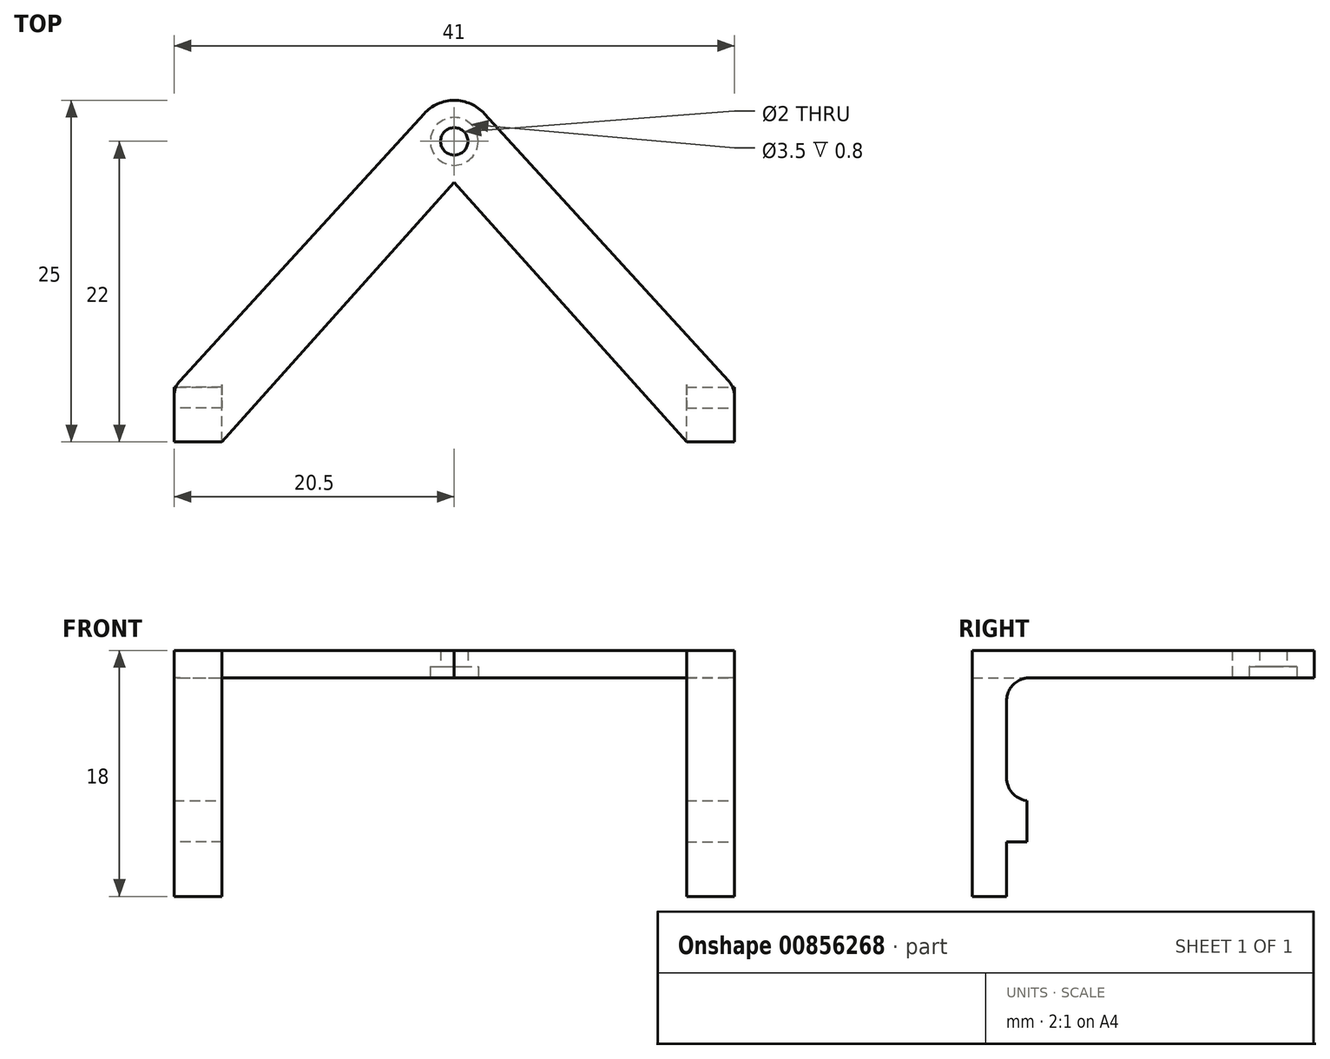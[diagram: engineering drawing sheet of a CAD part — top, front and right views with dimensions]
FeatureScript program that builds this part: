
annotation { "Feature Type Name" : "Feature", "Feature Type Description" : "" }
export const myFeature = defineFeature(function(context is Context, id is Id, definition is map)
    precondition{}
    {
        {
            var Q0;
            Q0=qCreatedBy(makeId("Top.planeOp"),FACE);
            var sketch = newSketch(context, id + "F0", { "sketchPlane" : qUnion([Q0])});
            skLineSegment(sketch, "E0", {"start": v(0, 0) * mm, "end": v(0, 22) * mm, "construction": true});
            skPoint(sketch, "E1", {"position": v(0, 22) * mm});
            skCircle(sketch, "E2", {"center": v(0, 22) * mm, "radius": 3 * mm});
            skLineSegment(sketch, "E3", {"start": v(0, 0) * mm, "end": v(17, 0) * mm, "construction": true});
            skLineSegment(sketch, "E4.bottom", {"start": v(17, 0) * mm, "end": v(20.5, 0) * mm});
            skLineSegment(sketch, "E4.top", {"start": v(17, 4) * mm, "end": v(20.5, 4) * mm});
            skLineSegment(sketch, "E4.left", {"start": v(17, 0) * mm, "end": v(17, 4) * mm});
            skLineSegment(sketch, "E4.right", {"start": v(20.5, 0) * mm, "end": v(20.5, 4) * mm});
            skLineSegment(sketch, "E5", {"start": v(20.5, 4) * mm, "end": v(2.22, 24.02) * mm});
            skLineSegment(sketch, "E6", {"start": v(17, 0) * mm, "end": v(0, 19) * mm});
            skLineSegment(sketch, "E7.MirrorCS", {"start": v(-17, 0) * mm, "end": v(0, 19) * mm});
            skLineSegment(sketch, "E8.MirrorCS", {"start": v(-20.5, 4) * mm, "end": v(-2.22, 24.02) * mm});
            skLineSegment(sketch, "E9.MirrorCS", {"start": v(-17, 4) * mm, "end": v(-20.5, 4) * mm});
            skLineSegment(sketch, "E10.MirrorCS", {"start": v(-17, 0) * mm, "end": v(-17, 4) * mm});
            skLineSegment(sketch, "E11.MirrorCS", {"start": v(-20.5, 0) * mm, "end": v(-20.5, 4) * mm});
            skLineSegment(sketch, "E12.MirrorCS", {"start": v(-17, 0) * mm, "end": v(-20.5, 0) * mm});
            skSolve(sketch);
        }
        {
            var Q0;
            {var subQ1=sQuery(id+"F0.wireOp",EDGE,"E7.MirrorCS");Q0=makeQuery(id+"F0.imprint","IMPRINT",FACE,{"disambiguationData":[TD([[makeQuery(id+"F0.imprint","IMPRINT",EDGE,{"derivedFrom":subQ1}),1.0]])]});}
            var Q1;
            {var subQ0=sQuery(id+"F0.wireOp",EDGE,"E2");var subQ1=makeQuery(id+"F0.imprint","INTERSECT",VERTEX,{"derivedFrom":[subQ0,sQuery(id+"F0.wireOp",EDGE,"E5")]});Q1=makeQuery(id+"F0.imprint","IMPRINT",FACE,{"disambiguationData":[TD([[makeQuery(id+"F0.imprint","IMPRINT",EDGE,{"disambiguationData":[TD([[subQ1,-1.0]])],"derivedFrom":subQ0}),1.0]])]});}
            var Q2;
            Q2=makeQuery(id+"F0.imprint","IMPRINT",FACE,{"disambiguationData":[TD([[makeQuery(id+"F0.imprint","IMPRINT",EDGE,{"derivedFrom":sQuery(id+"F0.wireOp",EDGE,"E4.top")}),1.0]])]});
            var Q3;
            Q3=makeQuery(id+"F0.imprint","IMPRINT",FACE,{"disambiguationData":[TD([[makeQuery(id+"F0.imprint","IMPRINT",EDGE,{"derivedFrom":sQuery(id+"F0.wireOp",EDGE,"E9.MirrorCS")}),1.0]])]});
            var Q4;
            Q4=makeQuery(id+"F0.imprint","IMPRINT",FACE,{"disambiguationData":[TD([[makeQuery(id+"F0.imprint","IMPRINT",EDGE,{"derivedFrom":sQuery(id+"F0.wireOp",EDGE,"E4.bottom")}),1.0]])]});
            extrude(context, id + "F1", {"entities" : qUnion([Q0, Q1, Q2, Q3, Q4]), "depth" : 2 * mm, "offsetDistance" : 25.4 * mm});
        }
        {
            var Q0;
            Q0=sQuery(id+"F0.wireOp",VERTEX,"E1");
            var Q1;
            Q1=makeQuery(id+"F1.opExtrude","SWEPT_BODY",BODY,{"disambiguationData":[OSD([sQuery(id+"F0.wireOp",EDGE,"E2"),sQuery(id+"F0.wireOp",EDGE,"E4.bottom"),sQuery(id+"F0.wireOp",EDGE,"E4.right"),sQuery(id+"F0.wireOp",EDGE,"E5"),sQuery(id+"F0.wireOp",EDGE,"E6"),sQuery(id+"F0.wireOp",EDGE,"E7.MirrorCS"),sQuery(id+"F0.wireOp",EDGE,"E8.MirrorCS"),sQuery(id+"F0.wireOp",EDGE,"E11.MirrorCS"),sQuery(id+"F0.wireOp",EDGE,"E12.MirrorCS")])]});
            hole(context, id + "F2", {"style" : HoleStyle.C_BORE, "endStyle" : HoleEndStyle.THROUGH, "oppositeDirection" : true, "holeDiameter" : 2 * mm, "cBoreDiameter" : 3.5 * mm, "cBoreDepth" : .8 * mm, "majorDiameter" : 6.35 * mm, "isTappedThrough" : true, "tappedDepth" : 12.7 * mm, "tapClearance" : 3, "locations" : qUnion([Q0]), "scope" : qUnion([Q1])});
        }
        {
            var Q0;
            Q0=makeQuery(id+"F0.imprint","IMPRINT",FACE,{"disambiguationData":[TD([[makeQuery(id+"F0.imprint","IMPRINT",EDGE,{"derivedFrom":sQuery(id+"F0.wireOp",EDGE,"E4.bottom")}),1.0]])]});
            var Q1;
            Q1=makeQuery(id+"F0.imprint","IMPRINT",FACE,{"disambiguationData":[TD([[makeQuery(id+"F0.imprint","IMPRINT",EDGE,{"derivedFrom":sQuery(id+"F0.wireOp",EDGE,"E9.MirrorCS")}),1.0]])]});
            extrude(context, id + "F3", {"entities" : qUnion([Q0, Q1]), "operationType" : NewBodyOperationType.ADD, "oppositeDirection" : true, "depth" : 12 * mm, "offsetDistance" : 25.4 * mm});
        }
        {
            var Q0;
            {var subQ0=sQuery(id+"F0.wireOp",EDGE,"E4.right");Q0=makeQuery(id+"F3.boolean.opBoolean","MERGE",FACE,{"derivedFrom":[makeQuery(id+"F1.opExtrude","SWEPT_FACE",FACE,{"disambiguationData":[OSD([subQ0])]}),makeQuery(id+"F3.opExtrude","SWEPT_FACE",FACE,{"disambiguationData":[OSD([subQ0])]})]});}
            var sketch = newSketch(context, id + "F4", { "sketchPlane" : qUnion([Q0])});
            skLineSegment(sketch, "E13.0.0", {"start": v(0, 2) * mm, "end": v(0, -12) * mm});
            skLineSegment(sketch, "E13.0.1", {"start": v(0, -12) * mm, "end": v(4, -12) * mm});
            skLineSegment(sketch, "E13.0.2", {"start": v(4, -12) * mm, "end": v(4, 0) * mm});
            skLineSegment(sketch, "E13.0.3", {"start": v(4, 0) * mm, "end": v(4, 2) * mm});
            skLineSegment(sketch, "E13.0.4", {"start": v(4, 2) * mm, "end": v(0, 2) * mm});
            skLineSegment(sketch, "E14", {"start": v(4, -12) * mm, "end": v(4, -9) * mm});
            skLineSegment(sketch, "E15", {"start": v(4, -9) * mm, "end": v(2.5, -8.75) * mm});
            skLineSegment(sketch, "E16", {"start": v(2.5, -8.75) * mm, "end": v(2.5, 0) * mm});
            skLineSegment(sketch, "E17", {"start": v(2.5, 0) * mm, "end": v(4, 0) * mm});
            skLineSegment(sketch, "E18", {"start": v(2.5, -8.75) * mm, "end": v(2.5, -12) * mm, "construction": true});
            skLineSegment(sketch, "E19", {"start": v(4, 0) * mm, "end": v(2.5, 0) * mm});
            skSolve(sketch);
        }
        {
            var Q0;
            Q0=makeQuery(id+"F4.imprint","IMPRINT",FACE,{"disambiguationData":[TD([[makeQuery(id+"F4.imprint","IMPRINT",EDGE,{"derivedFrom":sQuery(id+"F4.wireOp",EDGE,"E13.0.2")}),1.0]])]});
            extrude(context, id + "F5", {"entities" : qUnion([Q0]), "operationType" : NewBodyOperationType.REMOVE, "endBound" : BoundingType.THROUGH_ALL, "oppositeDirection" : true, "depth" : 25 * mm, "offsetDistance" : 25 * mm});
        }
        {
            var Q0;
            Q0=makeQuery(id+"F1.opExtrude","SWEPT_EDGE",EDGE,{"disambiguationData":[OSD([sQuery(id+"F0.wireOp",EDGE,"E4.top"),sQuery(id+"F0.wireOp",EDGE,"E4.right"),sQuery(id+"F0.wireOp",EDGE,"E5")])]});
            var Q1;
            Q1=makeQuery(id+"F1.opExtrude","SWEPT_EDGE",EDGE,{"disambiguationData":[OSD([sQuery(id+"F0.wireOp",EDGE,"E8.MirrorCS"),sQuery(id+"F0.wireOp",EDGE,"E9.MirrorCS"),sQuery(id+"F0.wireOp",EDGE,"E11.MirrorCS")])]});
            var Q2;
            Q2=makeQuery(id+"F3.opExtrude","CAP_EDGE",EDGE,{"disambiguationData":[OSD([sQuery(id+"F0.wireOp",EDGE,"E10.MirrorCS")])],"isStart":true});
            var Q3;
            {var subQ0=sQuery(id+"F0.wireOp",EDGE,"E11.MirrorCS");var subQ1=sQuery(id+"F4.wireOp",EDGE,"E16");var subQ2=sQuery(id+"F4.wireOp",EDGE,"E19");Q3=makeQuery(id+"F5.boolean.opBoolean","COPY",EDGE,{"disambiguationData":[TD([makeQuery(id+"F1.opExtrude","SWEPT_FACE",FACE,{"disambiguationData":[OSD([subQ0])]})])],"derivedFrom":makeQuery(id+"F5.opExtrude","SWEPT_EDGE",EDGE,{"disambiguationData":[OSD([subQ1,subQ2])]})});}
            var Q4;
            {var subQ0=sQuery(id+"F0.wireOp",EDGE,"E4.right");var subQ1=sQuery(id+"F4.wireOp",EDGE,"E19");var subQ2=sQuery(id+"F4.wireOp",EDGE,"E16");Q4=makeQuery(id+"F5.boolean.opBoolean","COPY",EDGE,{"disambiguationData":[TD([makeQuery(id+"F1.opExtrude","SWEPT_FACE",FACE,{"disambiguationData":[OSD([subQ0])]})])],"derivedFrom":makeQuery(id+"F5.opExtrude","SWEPT_EDGE",EDGE,{"disambiguationData":[OSD([subQ2,subQ1])]})});}
            var Q5;
            Q5=makeQuery(id+"F3.opExtrude","CAP_EDGE",EDGE,{"disambiguationData":[OSD([sQuery(id+"F0.wireOp",EDGE,"E4.left")])],"isStart":true});
            fillet(context, id + "F6", {"entities" : qUnion([Q0, Q1, Q2, Q3, Q4, Q5]), "radius" : 1.69 * mm, "tangentPropagation" : true, "allowEdgeOverflow" : false});
        }
        {
            var Q0;
            Q0=makeQuery(id+"F3.opExtrude","CAP_FACE",FACE,{"disambiguationData":[OSD([sQuery(id+"F0.wireOp",EDGE,"E4.bottom"),sQuery(id+"F0.wireOp",EDGE,"E4.top"),sQuery(id+"F0.wireOp",EDGE,"E4.left"),sQuery(id+"F0.wireOp",EDGE,"E4.right")])],"isStart":false});
            var sketch = newSketch(context, id + "F7", { "sketchPlane" : qUnion([Q0])});
            skLineSegment(sketch, "E20.bottom", {"start": v(17, 0) * mm, "end": v(20.5, 0) * mm});
            skLineSegment(sketch, "E20.top", {"start": v(17, -2.5) * mm, "end": v(20.5, -2.5) * mm});
            skLineSegment(sketch, "E20.left", {"start": v(17, 0) * mm, "end": v(17, -2.5) * mm});
            skLineSegment(sketch, "E20.right", {"start": v(20.5, 0) * mm, "end": v(20.5, -2.5) * mm});
            skLineSegment(sketch, "E21.MirrorCS", {"start": v(-17, -2.5) * mm, "end": v(-20.5, -2.5) * mm});
            skLineSegment(sketch, "E22.MirrorCS", {"start": v(-20.5, 0) * mm, "end": v(-20.5, -2.5) * mm});
            skLineSegment(sketch, "E23.MirrorCS", {"start": v(-17, 0) * mm, "end": v(-17, -2.5) * mm});
            skLineSegment(sketch, "E24.MirrorCS", {"start": v(-17, 0) * mm, "end": v(-20.5, 0) * mm});
            skSolve(sketch);
        }
        {
            var Q0;
            Q0=makeQuery(id+"F7.imprint","IMPRINT",FACE,{"disambiguationData":[TD([[makeQuery(id+"F7.imprint","IMPRINT",EDGE,{"derivedFrom":sQuery(id+"F7.wireOp",EDGE,"E20.bottom")}),-1.0]])]});
            var Q1;
            Q1=makeQuery(id+"F7.imprint","IMPRINT",FACE,{"disambiguationData":[TD([[makeQuery(id+"F7.imprint","IMPRINT",EDGE,{"derivedFrom":sQuery(id+"F7.wireOp",EDGE,"E21.MirrorCS")}),-1.0]])]});
            extrude(context, id + "F8", {"entities" : qUnion([Q0, Q1]), "operationType" : NewBodyOperationType.ADD, "depth" : 4 * mm, "offsetDistance" : 25 * mm});
        }
    });
